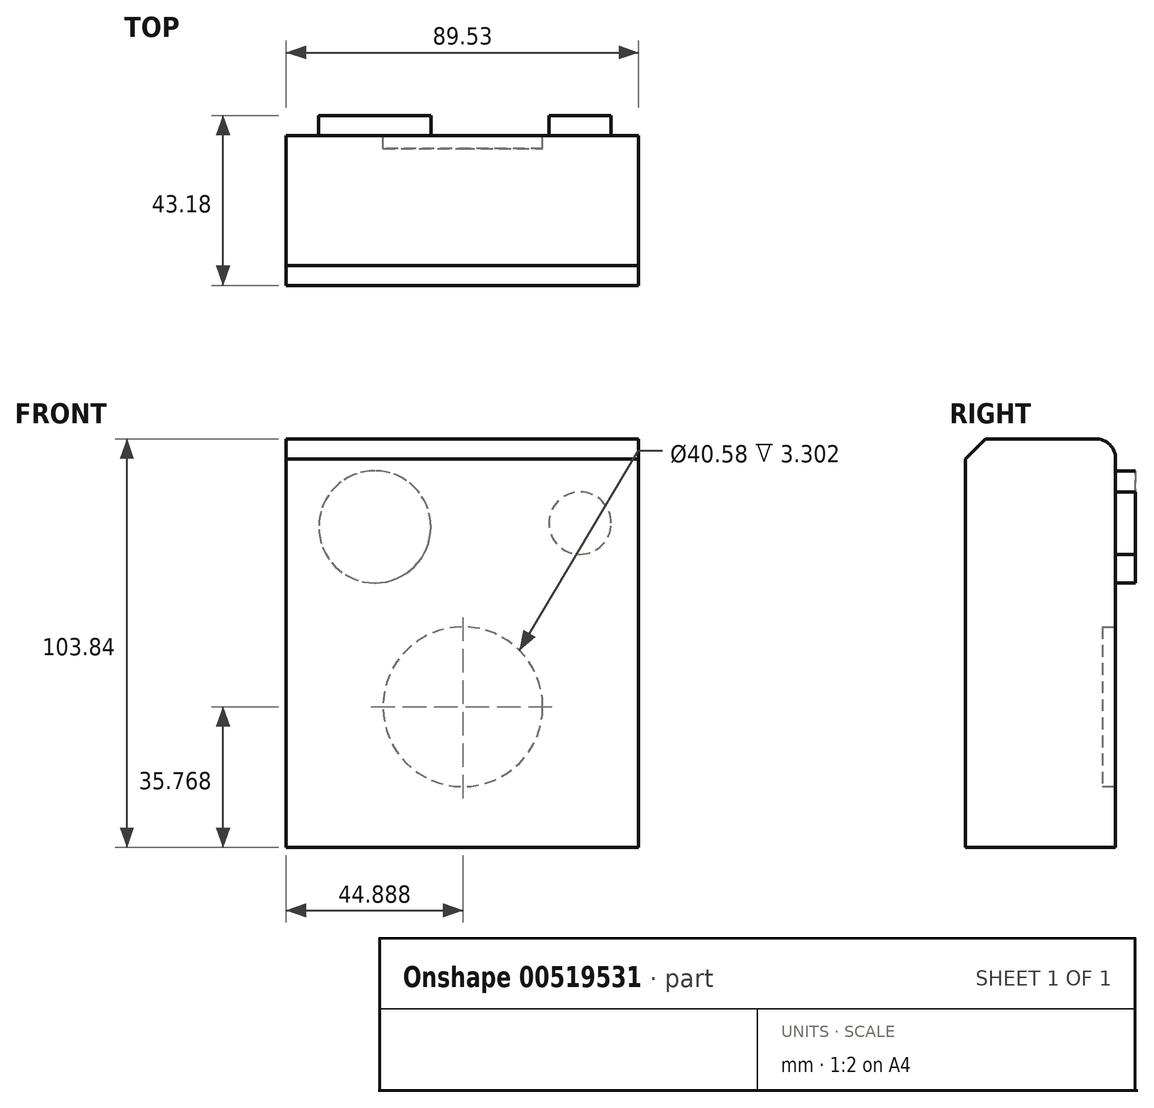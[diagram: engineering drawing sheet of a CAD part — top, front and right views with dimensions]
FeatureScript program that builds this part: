
annotation { "Feature Type Name" : "Feature", "Feature Type Description" : "" }
export const myFeature = defineFeature(function(context is Context, id is Id, definition is map)
    precondition{}
    {
        {
            var Q0;
            Q0=qCreatedBy(makeId("Front.planeOp"),FACE);
            var sketch = newSketch(context, id + "F0", { "sketchPlane" : qUnion([Q0])});
            skLineSegment(sketch, "E0.bottom", {"start": v(-77.66, 64.47) * mm, "end": v(11.87, 64.47) * mm});
            skLineSegment(sketch, "E0.top", {"start": v(-77.66, -39.37) * mm, "end": v(11.87, -39.37) * mm});
            skLineSegment(sketch, "E0.left", {"start": v(-77.66, 64.47) * mm, "end": v(-77.66, -39.37) * mm});
            skLineSegment(sketch, "E0.right", {"start": v(11.87, 64.47) * mm, "end": v(11.87, -39.37) * mm});
            skSolve(sketch);
        }
        {
            var Q0;
            Q0 = qSketchRegion(id + "F0", true);
            extrude(context, id + "F1", {"entities" : qUnion([Q0]), "depth" : 38.1 * mm, "offsetDistance" : 25.4 * mm});
        }
        {
            var Q0;
            Q0=makeQuery(id+"F1.opExtrude","CAP_EDGE",EDGE,{"disambiguationData":[OSD([sQuery(id+"F0.wireOp",EDGE,"E0.bottom")])],"isStart":false});
            chamfer(context, id + "F2", {"entities" : qUnion([Q0]), "width" : 5.08 * mm, "tangentPropagation" : true});
        }
        {
            var Q0;
            Q0=makeQuery(id+"F1.opExtrude","CAP_EDGE",EDGE,{"disambiguationData":[OSD([sQuery(id+"F0.wireOp",EDGE,"E0.bottom")])],"isStart":true});
            fillet(context, id + "F3", {"entities" : qUnion([Q0]), "radius" : 5.08 * mm, "tangentPropagation" : true, "allowEdgeOverflow" : false});
        }
        {
            var Q0;
            Q0=makeQuery(id+"F1.opExtrude","CAP_FACE",FACE,{"disambiguationData":[OSD([sQuery(id+"F0.wireOp",EDGE,"E0.bottom"),sQuery(id+"F0.wireOp",EDGE,"E0.top"),sQuery(id+"F0.wireOp",EDGE,"E0.left"),sQuery(id+"F0.wireOp",EDGE,"E0.right")])],"isStart":true});
            var sketch = newSketch(context, id + "F4", { "sketchPlane" : qUnion([Q0])});
            skCircle(sketch, "E1", {"center": v(32.77, -3.6) * mm, "radius": 20.29 * mm});
            skSolve(sketch);
        }
        {
            var Q0;
            Q0=makeQuery(id+"F4.imprint","IMPRINT",FACE,{"disambiguationData":[TD([[makeQuery(id+"F4.imprint","IMPRINT",EDGE,{"derivedFrom":sQuery(id+"F4.wireOp",EDGE,"E1")}),1.0]])]});
            extrude(context, id + "F5", {"entities" : qUnion([Q0]), "operationType" : NewBodyOperationType.REMOVE, "oppositeDirection" : true, "depth" : 3.3 * mm, "offsetDistance" : 25.4 * mm});
        }
        {
            var Q0;
            Q0=makeQuery(id+"F1.opExtrude","CAP_FACE",FACE,{"disambiguationData":[OSD([sQuery(id+"F0.wireOp",EDGE,"E0.bottom"),sQuery(id+"F0.wireOp",EDGE,"E0.top"),sQuery(id+"F0.wireOp",EDGE,"E0.left"),sQuery(id+"F0.wireOp",EDGE,"E0.right")])],"isStart":true});
            var sketch = newSketch(context, id + "F6", { "sketchPlane" : qUnion([Q0])});
            skCircle(sketch, "E2", {"center": v(3, 43.04) * mm, "radius": 7.91 * mm});
            skCircle(sketch, "E3", {"center": v(55.14, 42.1) * mm, "radius": 14.25 * mm});
            skSolve(sketch);
        }
        {
            var Q0;
            Q0 = qSketchRegion(id + "F6", true);
            extrude(context, id + "F7", {"entities" : qUnion([Q0]), "operationType" : NewBodyOperationType.ADD, "depth" : 5.08 * mm, "offsetDistance" : 25.4 * mm});
        }
    });
